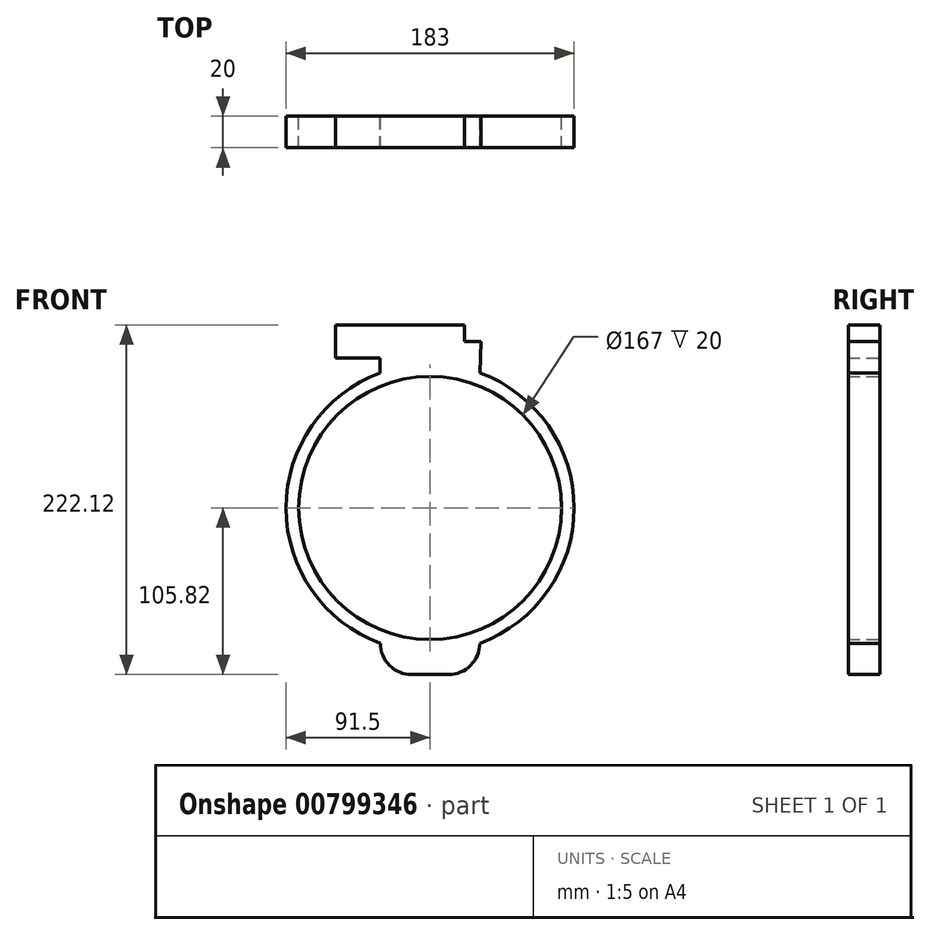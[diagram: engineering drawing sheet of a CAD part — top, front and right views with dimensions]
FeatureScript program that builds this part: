
annotation { "Feature Type Name" : "Feature", "Feature Type Description" : "" }
export const myFeature = defineFeature(function(context is Context, id is Id, definition is map)
    precondition{}
    {
        {
            var Q0;
            Q0=qCreatedBy(makeId("Front.planeOp"), FACE);
            var sketch = newSketch(context, id + "F0", { "sketchPlane" : qUnion([Q0])});
            skCircle(sketch, "E0", {"center": v(0, 0) * mm, "radius": 83.5 * mm});
            skLineSegment(sketch, "E1.bottom", {"start": v(-11.6, -105.82) * mm, "end": v(11.6, -105.82) * mm});
            skLineSegment(sketch, "E1.top", {"start": v(-31.7, 105.82) * mm, "end": v(0.35, 105.82) * mm});
            skPoint(sketch, "E2.visualSharp", {"position": v(-32.39, -105.82) * mm});
            skArc(sketch, "E2.filletArc", {"start": v(-31.6, -85.82) * mm, "mid": v(-25.75, -99.96) * mm, "end": v(-11.6, -105.82) * mm});
            skPoint(sketch, "E3.visualSharp", {"position": v(31.7, -105.82) * mm});
            skArc(sketch, "E3.filletArc", {"start": v(11.6, -105.82) * mm, "mid": v(25.75, -99.96) * mm, "end": v(31.6, -85.82) * mm});
            skLineSegment(sketch, "E4.bottom", {"start": v(-60.08, 95.34) * mm, "end": v(-31.7, 95.34) * mm});
            skLineSegment(sketch, "E4.top", {"start": v(-60.08, 116.3) * mm, "end": v(21.99, 116.3) * mm});
            skLineSegment(sketch, "E4.left", {"start": v(-60.08, 95.34) * mm, "end": v(-60.08, 116.3) * mm});
            skLineSegment(sketch, "E4.right", {"start": v(21.99, 105.82) * mm, "end": v(21.99, 116.3) * mm});
            skPoint(sketch, "E4.middle", {"position": v(-19.04, 105.82) * mm});
            skArc(sketch, "E5.0", {"start": v(31.6, -85.87) * mm, "mid": v(91.5, -0.05) * mm, "end": v(31.7, 85.83) * mm});
            skLineSegment(sketch, "E6.trimOffspring", {"start": v(-31.7, 85.83) * mm, "end": v(-31.7, 105.82) * mm});
            skLineSegment(sketch, "E7.trimOffspring", {"start": v(31.7, 85.83) * mm, "end": v(32.39, 105.82) * mm});
            skArc(sketch, "E8.trimOffspring", {"start": v(-31.7, 85.83) * mm, "mid": v(-91.5, -0.05) * mm, "end": v(-31.6, -85.87) * mm});
            skPoint(sketch, "E9.orphan", {"position": v(0.35, 105.82) * mm});
            skPoint(sketch, "E10.orphan", {"position": v(21.99, 95.34) * mm});
            skLineSegment(sketch, "E11.trimOffspring", {"start": v(21.99, 105.82) * mm, "end": v(32.39, 105.82) * mm});
            skSolve(sketch);
        }
        {
            var Q0;
            Q0 = qSketchRegion(id + "F0", true);
            extrude(context, id + "F1", {"entities" : qUnion([Q0]), "depth" : 20 * mm, "offsetDistance" : 25 * mm});
        }
    });
